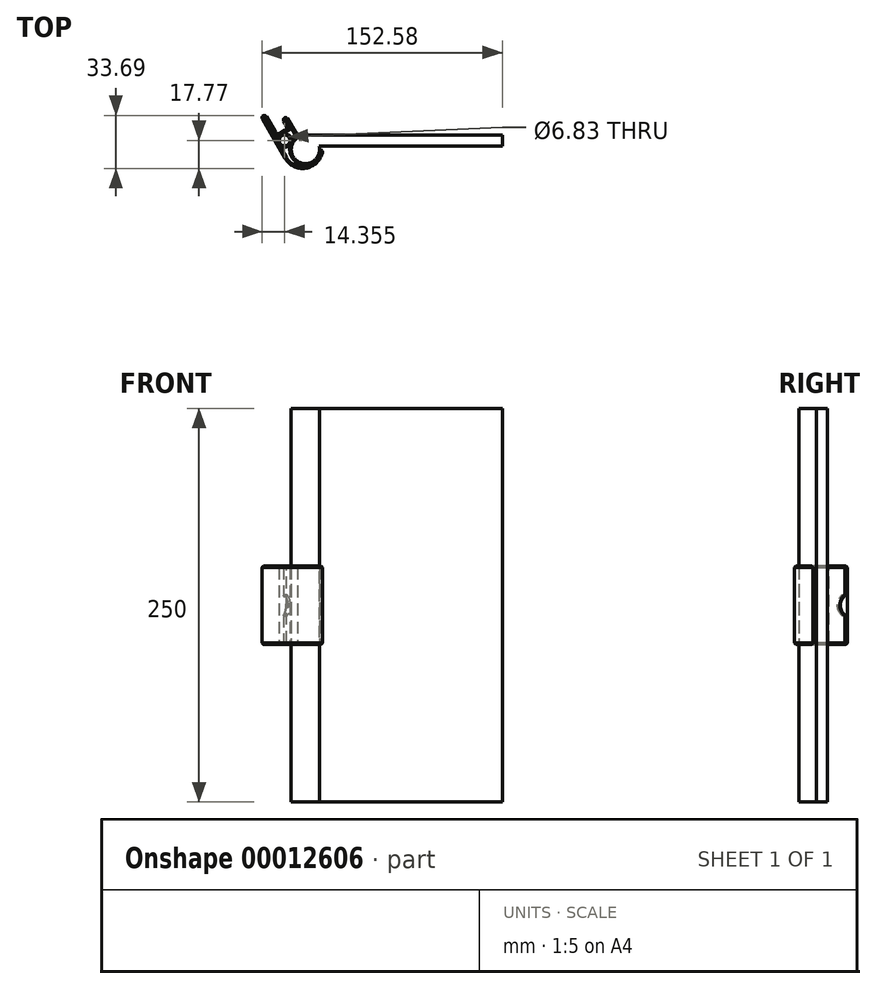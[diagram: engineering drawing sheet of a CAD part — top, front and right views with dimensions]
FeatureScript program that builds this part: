
annotation { "Feature Type Name" : "Feature", "Feature Type Description" : "" }
export const myFeature = defineFeature(function(context is Context, id is Id, definition is map)
    precondition{}
    {
        {
            var Q0;
            Q0=qCreatedBy(makeId("Top.planeOp"),FACE);
            var sketch = newSketch(context, id + "F0", { "sketchPlane" : qUnion([Q0])});
            skArc(sketch, "E0", {"start": v(9, 0) * mm, "mid": v(-4.5, -7.8) * mm, "end": v(-4.5, 7.8) * mm});
            skLineSegment(sketch, "E1", {"start": v(0, 0) * mm, "end": v(22.7, 0) * mm, "construction": true});
            skLineSegment(sketch, "E2", {"start": v(0, 0) * mm, "end": v(-19.43, 33.65) * mm, "construction": true});
            skLineSegment(sketch, "E3", {"start": v(9, 0) * mm, "end": v(11, 0) * mm});
            skLineSegment(sketch, "E4", {"start": v(-12.92, -5.61) * mm, "end": v(-28.12, 20.71) * mm});
            skLineSegment(sketch, "E5", {"start": v(-28.12, 20.71) * mm, "end": v(-25.53, 22.21) * mm});
            skLineSegment(sketch, "E6", {"start": v(-25.53, 22.21) * mm, "end": v(-18.03, 9.22) * mm});
            skLineSegment(sketch, "E7", {"start": v(-18.03, 9.22) * mm, "end": v(-11.1, 13.22) * mm});
            skLineSegment(sketch, "E8", {"start": v(-11.1, 13.22) * mm, "end": v(-14.6, 19.28) * mm});
            skLineSegment(sketch, "E9", {"start": v(-14.6, 19.28) * mm, "end": v(-12, 20.78) * mm});
            skArc(sketch, "E10", {"start": v(-12.92, -5.61) * mm, "mid": v(1.12, -11.7) * mm, "end": v(11, 0) * mm});
            skLineSegment(sketch, "E11", {"start": v(40.86, 23.59) * mm, "end": v(-39.8, -22.98) * mm, "construction": true});
            skLineSegment(sketch, "E12", {"start": v(-12, 20.78) * mm, "end": v(-4.5, 7.8) * mm});
            skCircle(sketch, "E13", {"center": v(-13.22, 5.74) * mm, "radius": 3.42 * mm});
            skSolve(sketch);
        }
        {
            var Q0;
            Q0 = qSketchRegion(id + "F0", true);
            extrude(context, id + "F1", {"entities" : qUnion([Q0]), "depth" : 50 * mm, "symmetric" : true});
        }
        {
            var Q0;
            Q0=makeQuery(id+"F1.opExtrude","SWEPT_EDGE",EDGE,{"disambiguationData":[OSD([sQuery(id+"F0.wireOp",EDGE,"E5"),sQuery(id+"F0.wireOp",EDGE,"E6")])]});
            var Q1;
            Q1=makeQuery(id+"F1.opExtrude","SWEPT_EDGE",EDGE,{"disambiguationData":[OSD([sQuery(id+"F0.wireOp",EDGE,"E4"),sQuery(id+"F0.wireOp",EDGE,"E5")])]});
            var Q2;
            Q2=makeQuery(id+"F1.opExtrude","SWEPT_EDGE",EDGE,{"disambiguationData":[OSD([sQuery(id+"F0.wireOp",EDGE,"E8"),sQuery(id+"F0.wireOp",EDGE,"E9")])]});
            var Q3;
            Q3=makeQuery(id+"F1.opExtrude","SWEPT_EDGE",EDGE,{"disambiguationData":[OSD([sQuery(id+"F0.wireOp",EDGE,"E9"),sQuery(id+"F0.wireOp",EDGE,"E12")])]});
            var Q4;
            Q4=makeQuery(id+"F1.opExtrude","SWEPT_EDGE",EDGE,{"disambiguationData":[OSD([sQuery(id+"F0.wireOp",EDGE,"E0"),sQuery(id+"F0.wireOp",EDGE,"E3")])]});
            var Q5;
            Q5=makeQuery(id+"F1.opExtrude","SWEPT_EDGE",EDGE,{"disambiguationData":[OSD([sQuery(id+"F0.wireOp",EDGE,"E3"),sQuery(id+"F0.wireOp",EDGE,"E10")])]});
            fillet(context, id + "F2", {"entities" : qUnion([Q0, Q1, Q2, Q3, Q4, Q5]), "radius" : 1.5 * mm, "tangentPropagation" : true, "allowEdgeOverflow" : false});
        }
        {
            var Q0;
            Q0=makeQuery(id+"F1.opExtrude","SWEPT_EDGE",EDGE,{"disambiguationData":[OSD([sQuery(id+"F0.wireOp",EDGE,"E0"),sQuery(id+"F0.wireOp",EDGE,"E12")])]});
            fillet(context, id + "F3", {"entities" : qUnion([Q0]), "radius" : 2 * mm, "tangentPropagation" : true, "allowEdgeOverflow" : false});
        }
        {
            var Q0;
            Q0=makeQuery(id+"F1.opExtrude","SWEPT_FACE",FACE,{"disambiguationData":[OSD([sQuery(id+"F0.wireOp",EDGE,"E12")])]});
            var sketch = newSketch(context, id + "F4", { "sketchPlane" : qUnion([Q0])});
            skCircle(sketch, "E14", {"center": v(27.5, 0) * mm, "radius": 7 * mm});
            skPoint(sketch, "E15", {"position": v(10.82, 0) * mm});
            skPoint(sketch, "E16", {"position": v(22.5, 0) * mm});
            skSolve(sketch);
        }
        {
            var Q0;
            Q0 = qSketchRegion(id + "F4", true);
            var Q1;
            Q1=makeQuery(id+"F1.opExtrude","SWEPT_FACE",FACE,{"disambiguationData":[OSD([sQuery(id+"F0.wireOp",EDGE,"E8")])]});
            extrude(context, id + "F5", {"entities" : qUnion([Q0]), "operationType" : NewBodyOperationType.REMOVE, "endBound" : BoundingType.UP_TO_SURFACE, "oppositeDirection" : true, "endBoundEntityFace" : qUnion([Q1]), "depth" : 25 * mm});
        }
        {
            var Q0;
            Q0=makeQuery(id+"F1.opExtrude","CAP_FACE",FACE,{"disambiguationData":[OSD([sQuery(id+"F0.wireOp",EDGE,"E0"),sQuery(id+"F0.wireOp",EDGE,"E3"),sQuery(id+"F0.wireOp",EDGE,"E4"),sQuery(id+"F0.wireOp",EDGE,"E5"),sQuery(id+"F0.wireOp",EDGE,"E6"),sQuery(id+"F0.wireOp",EDGE,"E7"),sQuery(id+"F0.wireOp",EDGE,"E8"),sQuery(id+"F0.wireOp",EDGE,"E9"),sQuery(id+"F0.wireOp",EDGE,"E10"),sQuery(id+"F0.wireOp",EDGE,"E12")])],"isStart":false});
            var Q1;
            Q1=makeQuery(id+"F1.opExtrude","CAP_FACE",FACE,{"disambiguationData":[OSD([sQuery(id+"F0.wireOp",EDGE,"E0"),sQuery(id+"F0.wireOp",EDGE,"E3"),sQuery(id+"F0.wireOp",EDGE,"E4"),sQuery(id+"F0.wireOp",EDGE,"E5"),sQuery(id+"F0.wireOp",EDGE,"E6"),sQuery(id+"F0.wireOp",EDGE,"E7"),sQuery(id+"F0.wireOp",EDGE,"E8"),sQuery(id+"F0.wireOp",EDGE,"E9"),sQuery(id+"F0.wireOp",EDGE,"E10"),sQuery(id+"F0.wireOp",EDGE,"E12")])],"isStart":true});
            chamfer(context, id + "F6", {"entities" : qUnion([Q0, Q1]), "width" : 0.95 * mm, "tangentPropagation" : true});
        }
        {
            var Q0;
            Q0=makeQuery(id+"F1.opExtrude","SWEPT_EDGE",EDGE,{"disambiguationData":[OSD([sQuery(id+"F0.wireOp",EDGE,"E6"),sQuery(id+"F0.wireOp",EDGE,"E7")])]});
            var Q1;
            Q1=makeQuery(id+"F1.opExtrude","SWEPT_EDGE",EDGE,{"disambiguationData":[OSD([sQuery(id+"F0.wireOp",EDGE,"E7"),sQuery(id+"F0.wireOp",EDGE,"E8")])]});
            fillet(context, id + "F7", {"entities" : qUnion([Q0, Q1]), "radius" : 2 * mm, "tangentPropagation" : true, "allowEdgeOverflow" : false});
        }
        {
            var Q0;
            Q0=qCreatedBy(makeId("Top.planeOp"),FACE);
            var sketch = newSketch(context, id + "F8", { "sketchPlane" : qUnion([Q0])});
            skCircle(sketch, "E17", {"center": v(0, 0) * mm, "radius": 9 * mm});
            skLineSegment(sketch, "E18.bottom", {"start": v(0, 9) * mm, "end": v(125, 9) * mm});
            skLineSegment(sketch, "E18.top", {"start": v(0, 2.14) * mm, "end": v(125, 2.14) * mm});
            skLineSegment(sketch, "E18.left", {"start": v(0, 9) * mm, "end": v(0, 2.14) * mm});
            skLineSegment(sketch, "E18.right", {"start": v(125, 9) * mm, "end": v(125, 2.14) * mm});
            skLineSegment(sketch, "E19", {"start": v(-32.62, 38.23) * mm, "end": v(28.74, -33.68) * mm, "construction": true});
            skSolve(sketch);
        }
        {
            var Q0;
            Q0 = qSketchRegion(id + "F8", true);
            extrude(context, id + "F9", {"entities" : qUnion([Q0]), "depth" : 250 * mm, "symmetric" : true});
        }
        {
            var Q0;
            Q0=makeQuery(id+"F5.boolean.opBoolean","COPY",FACE,{"derivedFrom":makeQuery(id+"F5.opExtrude","SWEPT_FACE",FACE,{"disambiguationData":[OSD([sQuery(id+"F4.wireOp",EDGE,"E14")])]})});
            chamfer(context, id + "F10", {"entities" : qUnion([Q0]), "width" : 1 * mm, "tangentPropagation" : true});
        }
    });
